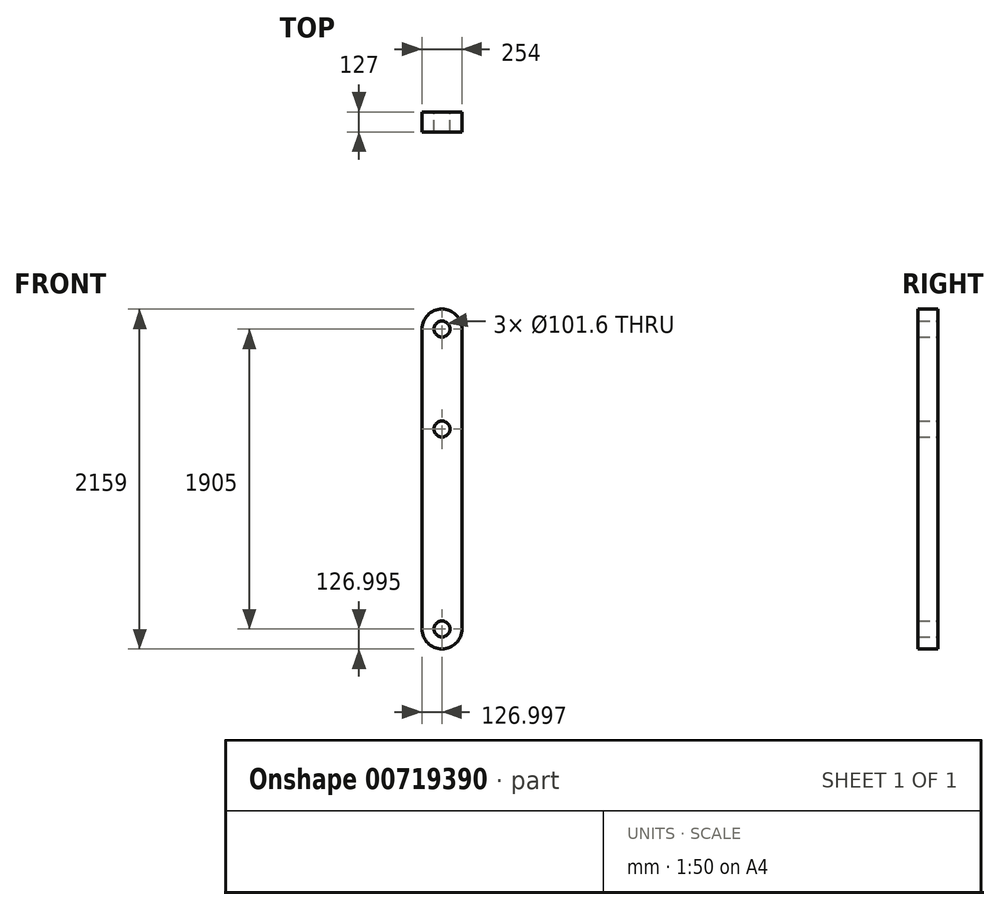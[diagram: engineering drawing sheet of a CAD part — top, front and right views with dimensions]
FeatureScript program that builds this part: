
annotation { "Feature Type Name" : "Feature", "Feature Type Description" : "" }
export const myFeature = defineFeature(function(context is Context, id is Id, definition is map)
    precondition{}
    {
        {
            var Q0;
            Q0=qCreatedBy(makeId("Front.planeOp"),FACE);
            var sketch = newSketch(context, id + "F0", { "sketchPlane" : qUnion([Q0])});
            skLineSegment(sketch, "E0", {"start": v(175.14, 958.37) * mm, "end": v(175.14, -946.63) * mm});
            skLineSegment(sketch, "E1", {"start": v(429.14, 958.37) * mm, "end": v(429.14, -946.63) * mm});
            skArc(sketch, "E2", {"start": v(429.14, 958.37) * mm, "mid": v(302.14, 1085.37) * mm, "end": v(175.14, 958.37) * mm});
            skArc(sketch, "E3", {"start": v(175.14, -946.63) * mm, "mid": v(302.14, -1073.63) * mm, "end": v(429.14, -946.63) * mm});
            skCircle(sketch, "E4", {"center": v(302.14, 958.37) * mm, "radius": 50.8 * mm});
            skCircle(sketch, "E5", {"center": v(302.14, -946.63) * mm, "radius": 50.8 * mm});
            skCircle(sketch, "E6", {"center": v(302.14, 323.37) * mm, "radius": 50.8 * mm});
            skSolve(sketch);
        }
        {
            var Q0;
            Q0 = qSketchRegion(id + "F0", true);
            extrude(context, id + "F1", {"entities" : qUnion([Q0]), "depth" : 127 * mm, "offsetDistance" : 25.4 * mm});
        }
    });
